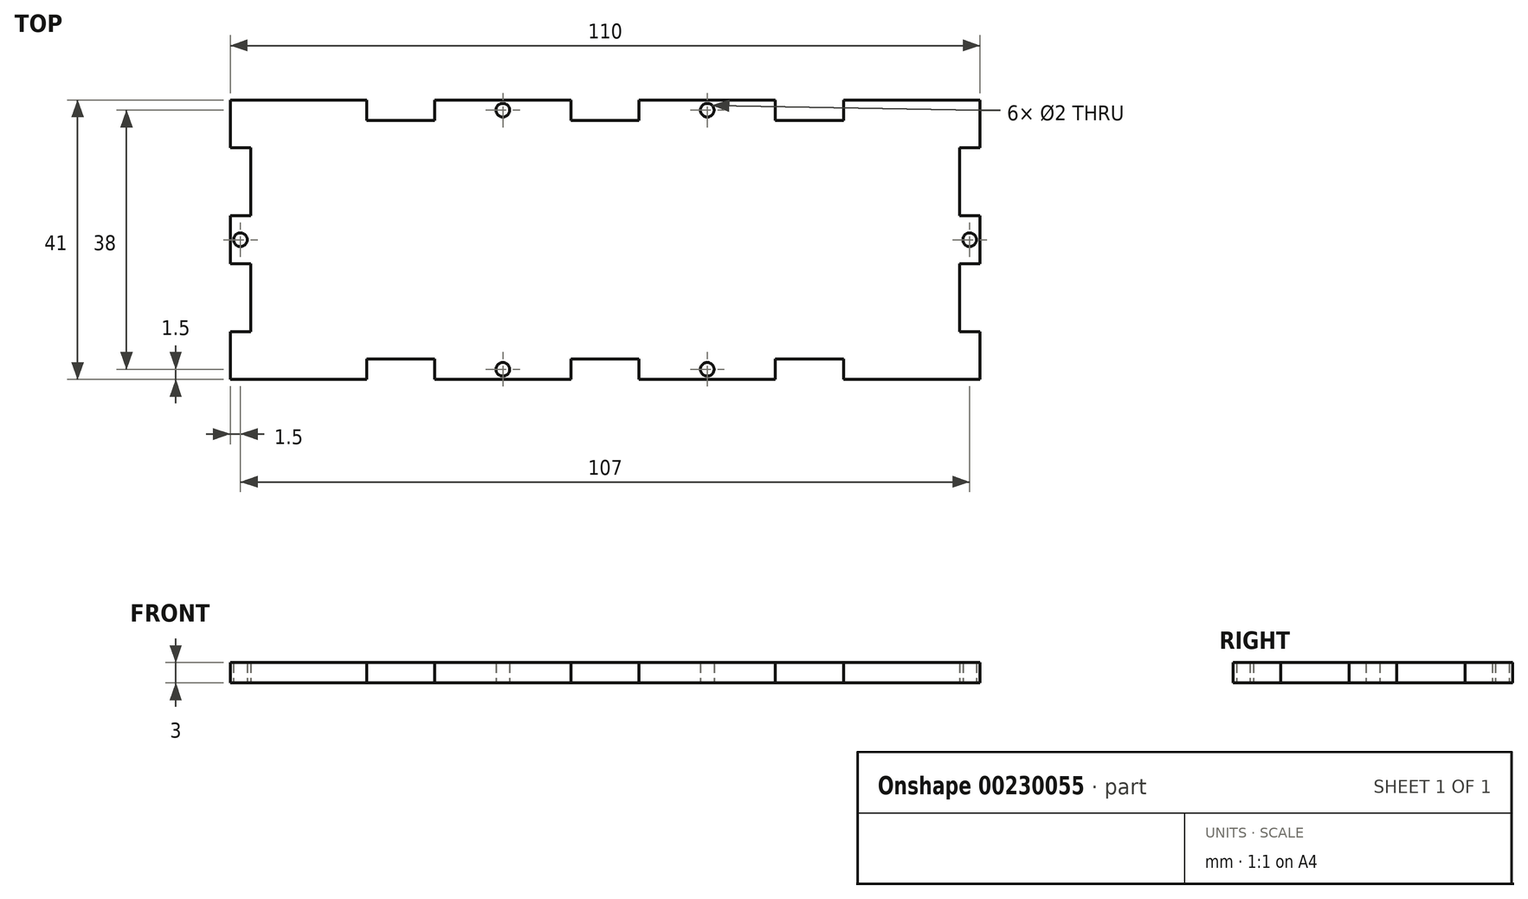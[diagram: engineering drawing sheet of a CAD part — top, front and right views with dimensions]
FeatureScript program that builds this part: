
annotation { "Feature Type Name" : "Feature", "Feature Type Description" : "" }
export const myFeature = defineFeature(function(context is Context, id is Id, definition is map)
    precondition{}
    {
        {
            var Q0;
            Q0=qCreatedBy(makeId("Top.planeOp"),FACE);
            var sketch = newSketch(context, id + "F0", { "sketchPlane" : qUnion([Q0])});
            skLineSegment(sketch, "E0", {"start": v(0, 0) * mm, "end": v(0, 7) * mm});
            skLineSegment(sketch, "E1", {"start": v(0, 7) * mm, "end": v(3, 7) * mm});
            skLineSegment(sketch, "E2", {"start": v(3, 7) * mm, "end": v(3, 17) * mm});
            skLineSegment(sketch, "E3", {"start": v(3, 17) * mm, "end": v(0, 17) * mm});
            skLineSegment(sketch, "E4", {"start": v(0, 17) * mm, "end": v(0, 24) * mm});
            skLineSegment(sketch, "E5", {"start": v(0, 24) * mm, "end": v(3, 24) * mm});
            skLineSegment(sketch, "E6", {"start": v(3, 34) * mm, "end": v(0, 34) * mm});
            skLineSegment(sketch, "E7", {"start": v(0, 34) * mm, "end": v(0, 41) * mm});
            skLineSegment(sketch, "E8", {"start": v(0, 41) * mm, "end": v(20, 41) * mm});
            skLineSegment(sketch, "E9", {"start": v(20, 41) * mm, "end": v(20, 38) * mm});
            skLineSegment(sketch, "E10", {"start": v(20, 38) * mm, "end": v(30, 38) * mm});
            skLineSegment(sketch, "E11", {"start": v(30, 38) * mm, "end": v(30, 41) * mm});
            skLineSegment(sketch, "E12", {"start": v(30, 41) * mm, "end": v(50, 41) * mm});
            skLineSegment(sketch, "E13", {"start": v(50, 41) * mm, "end": v(50, 38) * mm});
            skLineSegment(sketch, "E14", {"start": v(50, 38) * mm, "end": v(55, 38) * mm});
            skLineSegment(sketch, "E15", {"start": v(55, 38) * mm, "end": v(55, 3) * mm, "construction": true});
            skLineSegment(sketch, "E16", {"start": v(0, 0) * mm, "end": v(20, 0) * mm});
            skLineSegment(sketch, "E17", {"start": v(20, 0) * mm, "end": v(20, 3) * mm});
            skLineSegment(sketch, "E18", {"start": v(20, 3) * mm, "end": v(30, 3) * mm});
            skLineSegment(sketch, "E19", {"start": v(30, 3) * mm, "end": v(30, 0) * mm});
            skLineSegment(sketch, "E20", {"start": v(30, 0) * mm, "end": v(50, 0) * mm});
            skLineSegment(sketch, "E21", {"start": v(50, 0) * mm, "end": v(50, 3) * mm});
            skLineSegment(sketch, "E22", {"start": v(50, 3) * mm, "end": v(55, 3) * mm});
            skLineSegment(sketch, "E23.MirrorCS", {"start": v(80, 38) * mm, "end": v(80, 41) * mm});
            skLineSegment(sketch, "E24.MirrorCS", {"start": v(80, 3) * mm, "end": v(80, 0) * mm});
            skLineSegment(sketch, "E25.MirrorCS", {"start": v(90, 41) * mm, "end": v(90, 38) * mm});
            skLineSegment(sketch, "E26.MirrorCS", {"start": v(110, 24) * mm, "end": v(107, 24) * mm});
            skLineSegment(sketch, "E27.MirrorCS", {"start": v(90, 0) * mm, "end": v(90, 3) * mm});
            skLineSegment(sketch, "E28.MirrorCS", {"start": v(107, 34) * mm, "end": v(110, 34) * mm});
            skLineSegment(sketch, "E29.MirrorCS", {"start": v(110, 34) * mm, "end": v(110, 41) * mm});
            skLineSegment(sketch, "E30.MirrorCS", {"start": v(110, 17) * mm, "end": v(110, 24) * mm});
            skLineSegment(sketch, "E31.MirrorCS", {"start": v(60, 41) * mm, "end": v(60, 38) * mm});
            skLineSegment(sketch, "E32.MirrorCS", {"start": v(60, 38) * mm, "end": v(55, 38) * mm});
            skLineSegment(sketch, "E33.MirrorCS", {"start": v(107, 17) * mm, "end": v(110, 17) * mm});
            skLineSegment(sketch, "E34.MirrorCS", {"start": v(60, 0) * mm, "end": v(60, 3) * mm});
            skLineSegment(sketch, "E35.MirrorCS", {"start": v(110, 0) * mm, "end": v(110, 7) * mm});
            skLineSegment(sketch, "E36.MirrorCS", {"start": v(110, 7) * mm, "end": v(107, 7) * mm});
            skLineSegment(sketch, "E37.MirrorCS", {"start": v(60, 3) * mm, "end": v(55, 3) * mm});
            skLineSegment(sketch, "E38.MirrorCS", {"start": v(107, 7) * mm, "end": v(107, 17) * mm});
            skLineSegment(sketch, "E39.MirrorCS", {"start": v(90, 3) * mm, "end": v(80, 3) * mm});
            skLineSegment(sketch, "E40.MirrorCS", {"start": v(80, 0) * mm, "end": v(60, 0) * mm});
            skLineSegment(sketch, "E41.MirrorCS", {"start": v(107, 24) * mm, "end": v(107, 34) * mm});
            skLineSegment(sketch, "E42.MirrorCS", {"start": v(110, 41) * mm, "end": v(90, 41) * mm});
            skLineSegment(sketch, "E43.MirrorCS", {"start": v(110, 0) * mm, "end": v(90, 0) * mm});
            skLineSegment(sketch, "E44.MirrorCS", {"start": v(80, 41) * mm, "end": v(60, 41) * mm});
            skLineSegment(sketch, "E45.MirrorCS", {"start": v(90, 38) * mm, "end": v(80, 38) * mm});
            skPoint(sketch, "E46.centerSnap0", {"position": v(40, 41) * mm});
            skLineSegment(sketch, "E47", {"start": v(3, 34) * mm, "end": v(3, 24) * mm});
            skLineSegment(sketch, "E48.MirrorCS", {"start": v(55, 3) * mm, "end": v(55, 38) * mm, "construction": true});
            skCircle(sketch, "E49", {"center": v(1.5, 20.5) * mm, "radius": 1 * mm});
            skPoint(sketch, "E49.centerSnap0", {"position": v(1.5, 24) * mm});
            skPoint(sketch, "E49.centerSnap1", {"position": v(0, 20.5) * mm});
            skPoint(sketch, "E50.MirrorP", {"position": v(70, 41) * mm});
            skCircle(sketch, "E51.MirrorC", {"center": v(108.5, 20.5) * mm, "radius": 1 * mm});
            skPoint(sketch, "E52.MirrorP", {"position": v(110, 20.5) * mm});
            skPoint(sketch, "E53", {"position": v(70, 0) * mm});
            skCircle(sketch, "E54", {"center": v(40, 39.5) * mm, "radius": 1 * mm});
            skPoint(sketch, "E54.centerSnap0", {"position": v(50, 39.5) * mm});
            skCircle(sketch, "E55.MirrorC", {"center": v(40, 1.5) * mm, "radius": 1 * mm});
            skCircle(sketch, "E56.MirrorC", {"center": v(70, 1.5) * mm, "radius": 1 * mm});
            skCircle(sketch, "E57.MirrorC", {"center": v(70, 39.5) * mm, "radius": 1 * mm});
            skPoint(sketch, "E58.centerSnap0", {"position": v(85, 38) * mm});
            skPoint(sketch, "E59.centerSnap0", {"position": v(25, 38) * mm});
            skSolve(sketch);
        }
        {
            var Q0;
            Q0=qSketchRegion(id+"F0",true);
            extrude(context, id + "F1", {"entities" : qUnion([Q0]), "depth" : 3 * mm});
        }
    });
